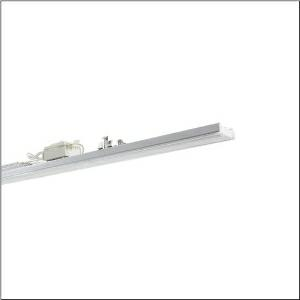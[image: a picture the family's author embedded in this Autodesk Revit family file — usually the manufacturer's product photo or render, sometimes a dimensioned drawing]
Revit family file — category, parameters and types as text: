
# Revit family: licross_11_recessed_mo_51tl18mn495g
name_source: partatom
category: Lighting Fixtures
units: mm (PartAtom-declared; Revit-internal decimal feet)

## family parameters
Cut with Voids When Loaded = No
Host = Face
Light Source = No
Part Type = Normal
Room Calculation Point = No
Round Connector Dimension = Use Diameter
Shared = No

## types (1)
- --- (1 x LED, 9990 lm, 55.2 W, 4000K)
    Apparent Load = 55 VA
    CIE Flux Codes = 83 96 99 100 100
    Color Rendering = 80
    Color Temperature = 4000K
    Default Elevation = 1800 mm
    Description = Licross 11 Recessed MO, luminaire insert, of sheet steel, coil coated, white, length: 1.500mm, width: 66mm, height: 67mm, LED rated luminous flux: 9.990lm, light colour: 840, SDCM (Standard Deviation of Colour Matching)MacAdam ≤ 2 SDCM (initial), control gear: ON/OFF Multilumen, with plug, 3-pole, with phase selection, mains connection: 220..240V, AC, 50/60Hz, rated input power: 55W, internal wiring halogen-free, primary light control with lens, of plastic, primary optical cover: cover, of PMMA, light emission: direct distribution, primary light characteristic: symmetric, protection rating (complete): IP40, insulation class (complete): insulation class I (protective earthing), certification: CE, ENEC, VDE, UKCA, protection symbol: D if used in an environment without relevant dust loads with corresponding accessories, impact resistance: IK06, permissible ambient temperature for indoor applications: -35..+40°C, corresponds to IFS (International Featured Standards) requirements for safety and quality in the food industry, reducing of maximum allowable ambient temperature of 5°C with ceiling mounting, The light source and the operating device comply with the requirements of the Ecodesign Regulation (EU) 2019/2020 and are replaceable in accordance with this regulation, packaging unit: 1 piece
    Height = 58 mm
    Lamp = 1 x LED
    Lamp Light Flux = 9990 lm
    Lamp Power = 55.2 W
    Lamp count = 1
    Length = 1500 mm
    Luminous efficacy = 181 lm/W
    Manufacturer = Siteco
    ModVariant = No
    Model = 51TL18MN495G
    Mounting Place = Ceiling
    Mounting Type = Pendant
    Number of Poles = 1
    OnlyDefault = Yes
    Power Factor = 1
    Product Name = Licross 11 Recessed MO
    Product group = luminaire insert | ceiling pendant
    ProductGroupID = 901
    Protection Class = Protection class I
    Protection Degree = IP 40
    RLX_Detail_Level = 1
    RLX_Emergency_Light_Flux = 0 lm
    RLX_Emergency_Type = 0
    RLX_Emergency_Type_DB = No
    RlxData = <blob elided: 22389 chars, md5=6e991d75>
    Socket = socket
    Standby Power = 0 W
    System Light Flux = 9990 lm
    System Power = 55 W
    Type Comments = factory setting: luminous flux: 100 % | (A | C | E) | 126 mA
    Type Image = l_1296930.jpg
    URL = http://relux.com
    VarID = @adj_089535
    Voltage = 0 V
    Weight = 0.00 kg
    Width = 66 mm

## geometry (parser evidence)
native form markers: Blend x4, Sweep x10
no freeform markers — native parametric forms only
